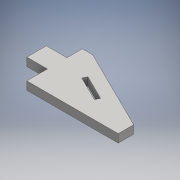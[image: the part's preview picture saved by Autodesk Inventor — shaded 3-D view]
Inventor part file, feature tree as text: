
AUTODESK INVENTOR PART (.ipt)
format: ipt  version: 2016 SP1 (Build 200210100, 210)  size: 114,688 bytes
history: native  units: mm
features: extrude x2, sketch x2
ambient origin geometry x8: Origin, YZ Plane, XZ Plane, XY Plane, X Axis, Y Axis, Z Axis, Center Point
bodies: Solid1 (feature_tree)
feature tree (4):
  extrude  "Extrusion1"  Depth=19.0mm
  extrude  "Extrusion3"  Depth=8.0mm
  sketch  "Sketch1"  dims[d0=20.0mm d1=19.0mm]
  sketch  "Sketch2"  dims[d2=9.5mm d3=10.0mm d4=15.0mm d5=10.0mm d6=10.0mm d7=88.0mm d8=20.0mm d9=8.0mm d10=0.0mm d12=24.0mm d13=27.0mm d17=16.0mm d18=4.5mm d19=8.0mm d20=0.0mm]
